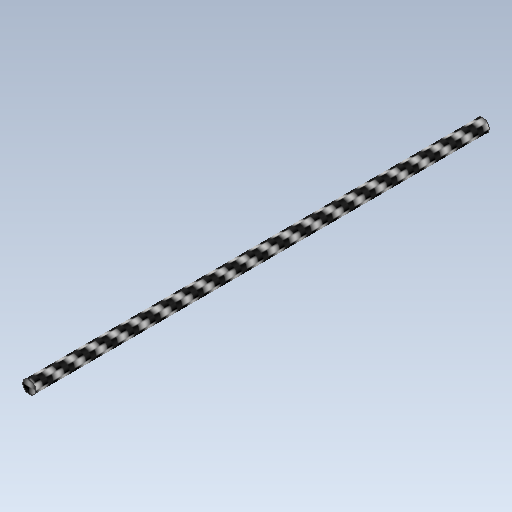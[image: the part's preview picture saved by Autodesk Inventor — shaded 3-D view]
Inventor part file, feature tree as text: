
AUTODESK INVENTOR PART (.ipt)
format: ipt  version: 2020 (Build 240168000, 168)  size: 108,544 bytes
history: native  units: in
note: dims shown in document units (in); Inventor stores cm internally (conversion verified against a paired STEP export)
features: extrude x1, sketch x1
ambient origin geometry x8: Origin, YZ Plane, XZ Plane, XY Plane, X Axis, Y Axis, Z Axis, Center Point
bodies: Solid1 (feature_tree)
feature tree (2):
  extrude  "Extrusion1"  Depth=3.1106in
  sketch  "Sketch1"  dims[d0=0.0906in d1=3.1106in d2=0.0in]
